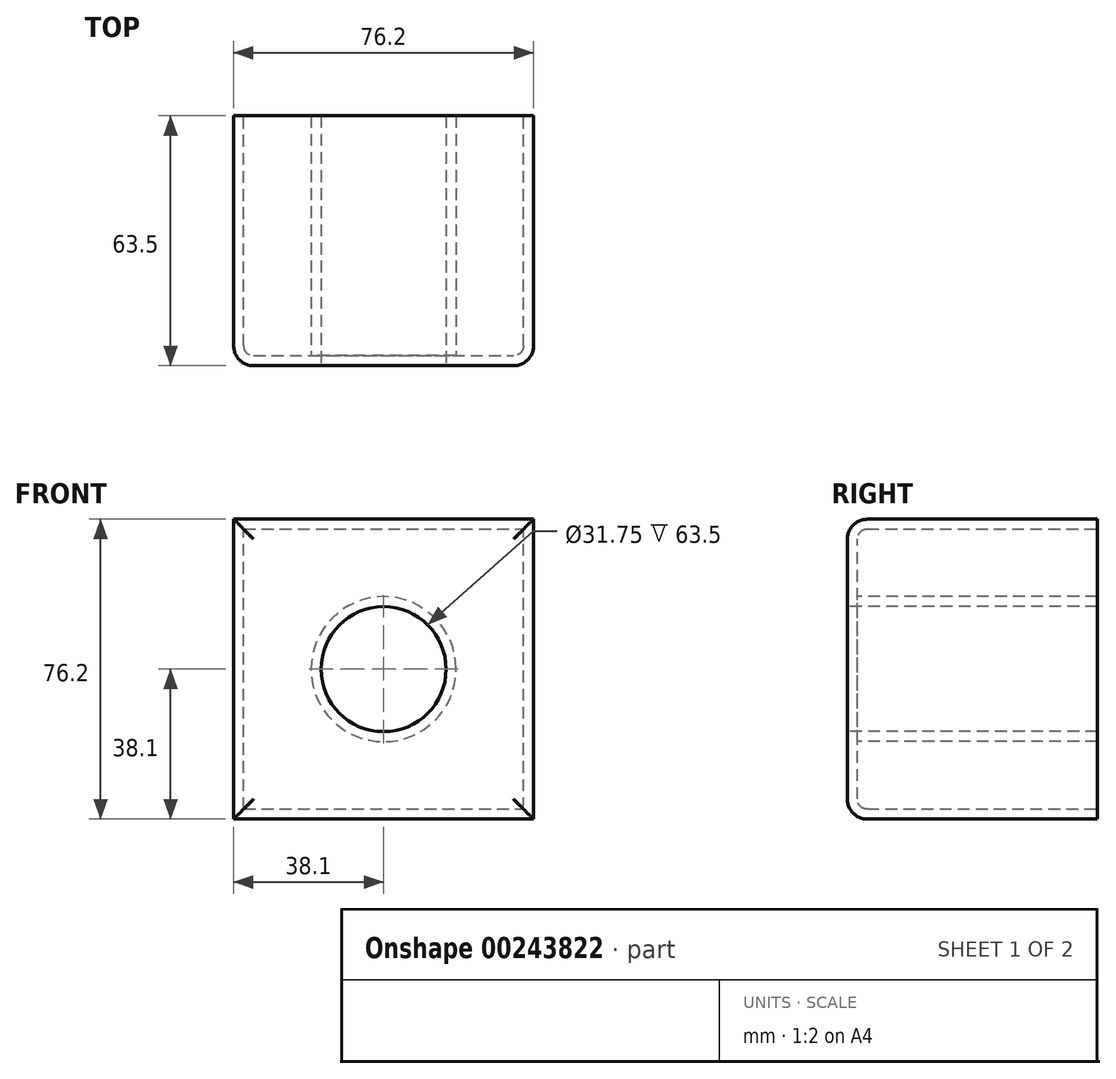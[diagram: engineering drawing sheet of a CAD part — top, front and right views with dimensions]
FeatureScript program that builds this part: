
annotation { "Feature Type Name" : "Feature", "Feature Type Description" : "" }
export const myFeature = defineFeature(function(context is Context, id is Id, definition is map)
    precondition{}
    {
        {
            var Q0;
            Q0=qCreatedBy(makeId("Front.planeOp"),FACE);
            var sketch = newSketch(context, id + "F3", { "sketchPlane" : qUnion([Q0])});
            skLineSegment(sketch, "E0.bottom", {"start": v(0, 0) * mm, "end": v(76.2, 0) * mm});
            skLineSegment(sketch, "E0.top", {"start": v(0, 76.2) * mm, "end": v(76.2, 76.2) * mm});
            skLineSegment(sketch, "E0.left", {"start": v(0, 0) * mm, "end": v(0, 76.2) * mm});
            skLineSegment(sketch, "E0.right", {"start": v(76.2, 0) * mm, "end": v(76.2, 76.2) * mm});
            skSolve(sketch);
        }
        {
            var Q0;
            Q0=makeQuery(id+"F3.imprint","IMPRINT",FACE,{"disambiguationData":[TD([[makeQuery(id+"F3.imprint","IMPRINT",EDGE,{"derivedFrom":sQuery(id+"F3.wireOp",EDGE,"E0.bottom")}),1.0]])]});
            extrude(context, id + "F0", {"entities" : qUnion([Q0]), "depth" : 63.5 * mm});
        }
        {
            var Q0;
            Q0=makeQuery(id+"F0.opExtrude","CAP_FACE",FACE,{"disambiguationData":[OSD([sQuery(id+"F3.wireOp",EDGE,"E0.bottom"),sQuery(id+"F3.wireOp",EDGE,"E0.top"),sQuery(id+"F3.wireOp",EDGE,"E0.left"),sQuery(id+"F3.wireOp",EDGE,"E0.right")])],"isStart":false});
            var sketch = newSketch(context, id + "F1", { "sketchPlane" : qUnion([Q0])});
            skCircle(sketch, "E1", {"center": v(38.1, 38.1) * mm, "radius": 15.88 * mm});
            skSolve(sketch);
        }
        {
            var Q0;
            Q0=makeQuery(id+"F1.imprint","IMPRINT",FACE,{"disambiguationData":[TD([[makeQuery(id+"F1.imprint","IMPRINT",EDGE,{"derivedFrom":sQuery(id+"F1.wireOp",EDGE,"E1")}),1.0]])]});
            extrude(context, id + "F2", {"entities" : qUnion([Q0]), "operationType" : NewBodyOperationType.REMOVE, "endBound" : BoundingType.THROUGH_ALL, "oppositeDirection" : true, "depth" : 25.4 * mm});
        }
        {
            var Q0;
            Q0=makeQuery(id+"F0.opExtrude","CAP_EDGE",EDGE,{"disambiguationData":[OSD([sQuery(id+"F3.wireOp",EDGE,"E0.left")])],"isStart":false});
            var Q1;
            Q1=makeQuery(id+"F0.opExtrude","CAP_EDGE",EDGE,{"disambiguationData":[OSD([sQuery(id+"F3.wireOp",EDGE,"E0.top")])],"isStart":false});
            var Q2;
            Q2=makeQuery(id+"F0.opExtrude","CAP_EDGE",EDGE,{"disambiguationData":[OSD([sQuery(id+"F3.wireOp",EDGE,"E0.right")])],"isStart":false});
            var Q3;
            Q3=makeQuery(id+"F0.opExtrude","CAP_EDGE",EDGE,{"disambiguationData":[OSD([sQuery(id+"F3.wireOp",EDGE,"E0.bottom")])],"isStart":false});
            fillet(context, id + "F4", {"entities" : qUnion([Q0, Q1, Q2, Q3]), "radius" : 5.08 * mm, "tangentPropagation" : true, "allowEdgeOverflow" : false});
        }
        {
            var Q0;
            Q0=makeQuery(id+"F0.opExtrude","CAP_FACE",FACE,{"disambiguationData":[OSD([sQuery(id+"F3.wireOp",EDGE,"E0.bottom"),sQuery(id+"F3.wireOp",EDGE,"E0.top"),sQuery(id+"F3.wireOp",EDGE,"E0.left"),sQuery(id+"F3.wireOp",EDGE,"E0.right")])],"isStart":true});
            shell(context, id + "F5", {"entities" : qUnion([Q0]), "thickness" : 2.54 * mm});
        }
    });
